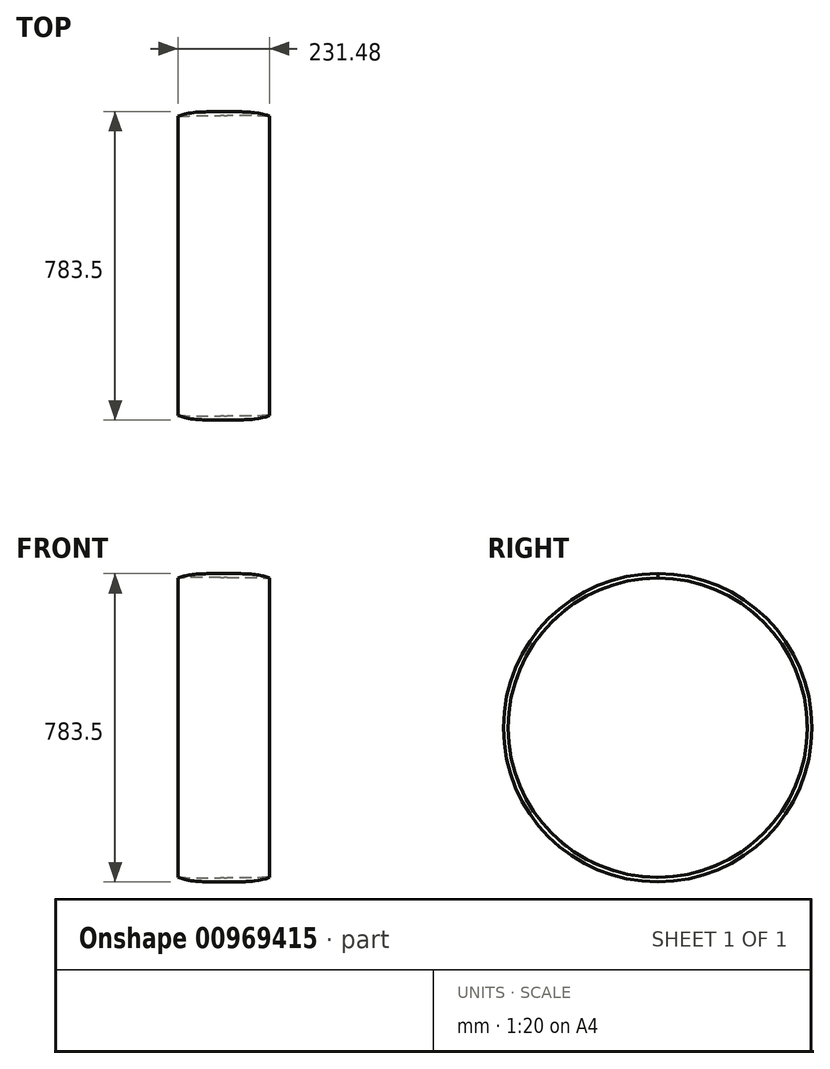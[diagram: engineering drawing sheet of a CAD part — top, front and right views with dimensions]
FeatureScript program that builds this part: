
annotation { "Feature Type Name" : "Feature", "Feature Type Description" : "" }
export const myFeature = defineFeature(function(context is Context, id is Id, definition is map)
    precondition{}
    {
        {
            var Q0;
            Q0=qCreatedBy(makeId("Right.planeOp"),FACE);
            var sketch = newSketch(context, id + "F0", { "sketchPlane" : qUnion([Q0])});
            skLineSegment(sketch, "E0", {"start": v(-925, 0) * mm, "end": v(925, 0) * mm, "construction": true});
            skSolve(sketch);
        }
        {
            var Q0;
            Q0=qCreatedBy(makeId("Front.planeOp"),FACE);
            cPlane(context, id + "F1", {"entities" : qUnion([Q0]), "cplaneType" : CPlaneType.OFFSET, "offset" : 925 * mm, "oppositeDirection" : true, "width" : 150 * mm, "height" : 150 * mm});
        }
        {
            var Q0;
            Q0=qCreatedBy(id+"F1.planeOp",FACE);
            var sketch = newSketch(context, id + "F2", { "sketchPlane" : qUnion([Q0])});
            skLineSegment(sketch, "E1.bottom", {"start": v(455, 783.5) * mm, "end": v(731, 783.5) * mm, "construction": true});
            skLineSegment(sketch, "E1.top", {"start": v(455, 0) * mm, "end": v(731, 0) * mm, "construction": true});
            skPoint(sketch, "E2.endSnap0", {"position": v(455, 391.75) * mm});
            skFitSpline(sketch, "E3", {"points": [v(731, 738.5) * mm, v(593, 783.5) * mm, v(352.76, 751.64) * mm], "startDerivative": vector(0, 309.44) * mm, "endDerivative": vector(-131.99, -169.56) * mm});
            skFitSpline(sketch, "E4", {"points": [v(731, 738.5) * mm, v(710.8, 607.6) * mm], "startDerivative": vector(0, -150) * mm, "endDerivative": vector(-66, -29.7) * mm});
            skLineSegment(sketch, "E5", {"start": v(593, 783.5) * mm, "end": v(593, 595.5) * mm, "construction": true});
            skLineSegment(sketch, "E6", {"start": v(455, 783.5) * mm, "end": v(455, 0) * mm, "construction": true});
            skLineSegment(sketch, "E7", {"start": v(455, 391.75) * mm, "end": v(842.94, 391.75) * mm, "construction": true});
            skLineSegment(sketch, "E8", {"start": v(593, 595.5) * mm, "end": v(455, 595.5) * mm, "construction": true});
            skLineSegment(sketch, "E9", {"start": v(731, 0) * mm, "end": v(731, 783.5) * mm, "construction": true});
            skFitSpline(sketch, "E10.0", {"points": [v(721, 738.5) * mm, v(721, 739.78) * mm, v(720.87, 742.18) * mm, v(720.35, 745.36) * mm, v(719.53, 748.17) * mm, v(718.43, 750.67) * mm, v(717.07, 752.96) * mm, v(715.39, 755.1) * mm, v(713.37, 757.12) * mm, v(710.16, 759.7) * mm, v(705.1, 762.67) * mm, v(697.37, 765.75) * mm, v(688.07, 768.26) * mm, v(677.39, 770.2) * mm, v(665.47, 771.6) * mm, v(652.48, 772.55) * mm, v(638.55, 773.12) * mm, v(623.82, 773.4) * mm, v(610.98, 773.49) * mm, v(600.43, 773.5) * mm, v(592.38, 773.5) * mm, v(584.24, 773.5) * mm, v(573.29, 773.5) * mm, v(559.44, 773.47) * mm, v(542.7, 773.36) * mm, v(520.36, 773.1) * mm, v(492.7, 772.44) * mm, v(460.9, 770.87) * mm, v(431.47, 768.28) * mm, v(409.77, 765.08) * mm, v(394.65, 761.82) * mm, v(384.58, 759) * mm, v(375.96, 755.86) * mm, v(368.96, 752.44) * mm, v(364.62, 749.48) * mm, v(362.06, 747.16) * mm, v(361.08, 746.04) * mm, v(360.65, 745.5) * mm]});
            skFitSpline(sketch, "E10.1", {"points": [v(721, 738.5) * mm, v(721, 732.22) * mm, v(721.06, 719.06) * mm, v(721, 698.45) * mm, v(720.54, 677.95) * mm, v(719.55, 661.79) * mm, v(718.28, 649.95) * mm, v(717.06, 641.77) * mm, v(715.56, 634.44) * mm, v(713.78, 628.14) * mm, v(712.12, 623.9) * mm, v(710.75, 621.24) * mm, v(709.74, 619.62) * mm, v(708.78, 618.39) * mm, v(707.94, 617.53) * mm, v(707.24, 617) * mm, v(706.87, 616.8) * mm, v(706.7, 616.72) * mm]});
            skLineSegment(sketch, "E11", {"start": v(708.2, 617.8) * mm, "end": v(697.72, 607.6) * mm});
            skFitSpline(sketch, "E12.MirrorCS", {"points": [v(455, 738.5) * mm, v(593, 783.5) * mm, v(833.24, 751.64) * mm], "startDerivative": vector(0, 309.44) * mm, "endDerivative": vector(131.99, -169.56) * mm});
            skFitSpline(sketch, "E13.MirrorCS", {"points": [v(455, 738.5) * mm, v(475.2, 607.6) * mm], "startDerivative": vector(0, -150) * mm, "endDerivative": vector(66, -29.7) * mm});
            skLineSegment(sketch, "E14.MirrorCS", {"start": v(477.8, 617.8) * mm, "end": v(488.28, 607.6) * mm});
            skFitSpline(sketch, "E15.MirrorCS", {"points": [v(465, 738.5) * mm, v(465, 732.22) * mm, v(464.94, 719.06) * mm, v(465, 698.45) * mm, v(465.46, 677.95) * mm, v(466.45, 661.79) * mm, v(467.72, 649.95) * mm, v(468.94, 641.77) * mm, v(470.44, 634.44) * mm, v(472.22, 628.14) * mm, v(473.88, 623.9) * mm, v(475.25, 621.24) * mm, v(476.26, 619.62) * mm, v(477.22, 618.39) * mm, v(478.06, 617.53) * mm, v(478.76, 617) * mm, v(479.13, 616.8) * mm, v(479.3, 616.72) * mm]});
            skFitSpline(sketch, "E16.MirrorCS", {"points": [v(465, 738.5) * mm, v(465, 739.78) * mm, v(465.13, 742.18) * mm, v(465.65, 745.36) * mm, v(466.47, 748.17) * mm, v(467.57, 750.67) * mm, v(468.93, 752.96) * mm, v(470.61, 755.1) * mm, v(472.63, 757.12) * mm, v(475.84, 759.7) * mm, v(480.9, 762.67) * mm, v(488.63, 765.75) * mm, v(497.93, 768.26) * mm, v(508.61, 770.2) * mm, v(520.53, 771.6) * mm, v(533.52, 772.55) * mm, v(547.45, 773.12) * mm, v(562.18, 773.4) * mm, v(575.02, 773.49) * mm, v(585.57, 773.5) * mm, v(593.62, 773.5) * mm, v(601.76, 773.5) * mm, v(612.71, 773.5) * mm, v(626.56, 773.47) * mm, v(643.3, 773.36) * mm, v(665.64, 773.1) * mm, v(693.3, 772.44) * mm, v(725.1, 770.87) * mm, v(754.53, 768.28) * mm, v(776.23, 765.08) * mm, v(791.35, 761.82) * mm, v(801.42, 759) * mm, v(810.04, 755.86) * mm, v(817.04, 752.44) * mm, v(821.38, 749.48) * mm, v(823.94, 747.16) * mm, v(824.92, 746.04) * mm, v(825.35, 745.5) * mm]});
            skLineSegment(sketch, "E17", {"start": v(475.2, 607.6) * mm, "end": v(488.28, 607.6) * mm});
            skPoint(sketch, "E18.orphan", {"position": v(495.7, 600.37) * mm});
            skPoint(sketch, "E19.2.internal.orphan", {"position": v(464.04, 607.6) * mm});
            skPoint(sketch, "E19.end.orphan", {"position": v(690.3, 600.37) * mm});
            skPoint(sketch, "E19.startDerivative.orphan", {"position": v(672.8, 590.5) * mm});
            skLineSegment(sketch, "E20.trimOffspring", {"start": v(697.72, 607.6) * mm, "end": v(710.8, 607.6) * mm});
            skPoint(sketch, "E21.orphan", {"position": v(593, 447.5) * mm});
            skSolve(sketch);
        }
        {
            var Q0;
            Q0=makeQuery(id+"F2.imprint","IMPRINT",FACE,{"disambiguationData":[TD([[makeQuery(id+"F2.imprint","IMPRINT",EDGE,{"derivedFrom":sQuery(id+"F2.wireOp",EDGE,"E3")}),1.0]])]});
            var Q1;
            Q1=sQuery(id+"F2.wireOp",EDGE,"E7");
            revolve(context, id + "F3", {"surfaceOperationType" : NewSurfaceOperationType.NEW, "entities" : qUnion([Q0]), "axis" : qUnion([Q1]), "revolveType" : RevolveType.FULL});
        }
    });
